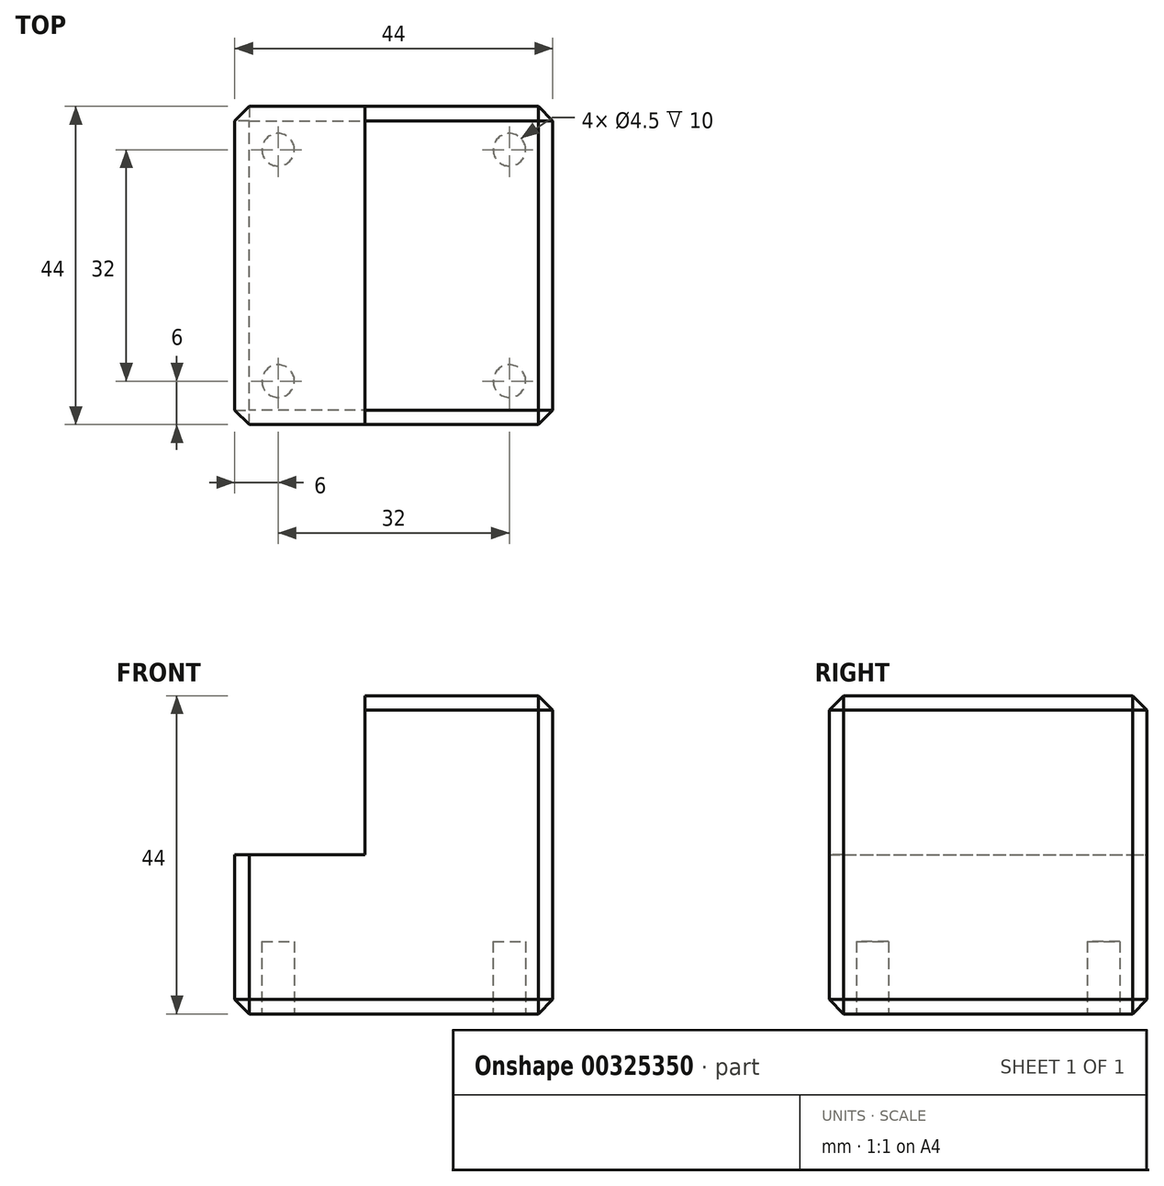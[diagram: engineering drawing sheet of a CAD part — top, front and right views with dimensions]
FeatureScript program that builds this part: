
annotation { "Feature Type Name" : "Feature", "Feature Type Description" : "" }
export const myFeature = defineFeature(function(context is Context, id is Id, definition is map)
    precondition{}
    {
        {
            var Q0;
            Q0=qCreatedBy(makeId("Front.planeOp"),FACE);
            var sketch = newSketch(context, id + "F0", { "sketchPlane" : qUnion([Q0])});
            skLineSegment(sketch, "E0.bottom", {"start": v(22, 22) * mm, "end": v(-4, 22) * mm});
            skLineSegment(sketch, "E0.top", {"start": v(22, -22) * mm, "end": v(-22, -22) * mm});
            skLineSegment(sketch, "E0.left", {"start": v(22, 22) * mm, "end": v(22, -22) * mm});
            skLineSegment(sketch, "E0.right", {"start": v(-22, 0) * mm, "end": v(-22, -22) * mm});
            skPoint(sketch, "E0.middle", {"position": v(0, 0) * mm});
            skLineSegment(sketch, "E1.top", {"start": v(-22, 0) * mm, "end": v(-4, 0) * mm});
            skLineSegment(sketch, "E1.right", {"start": v(-4, 22) * mm, "end": v(-4, 0) * mm});
            skPoint(sketch, "E2.orphan", {"position": v(-22, 22) * mm});
            skSolve(sketch);
        }
        {
            var Q0;
            Q0 = qSketchRegion(id + "F0", true);
            extrude(context, id + "F1", {"entities" : qUnion([Q0]), "depth" : 22 * mm, "hasSecondDirection" : true, "secondDirectionOppositeDirection" : true, "secondDirectionDepth" : 22 * mm});
        }
        {
            var Q0;
            Q0=makeQuery(id+"F1.opExtrude","SWEPT_EDGE",EDGE,{"disambiguationData":[OSD([sQuery(id+"F0.wireOp",EDGE,"E0.bottom"),sQuery(id+"F0.wireOp",EDGE,"E0.left")])]});
            var Q1;
            Q1=makeQuery(id+"F1.opExtrude","CAP_EDGE",EDGE,{"disambiguationData":[OSD([sQuery(id+"F0.wireOp",EDGE,"E0.bottom")])],"isStart":false});
            var Q2;
            Q2=makeQuery(id+"F1.opExtrude","CAP_EDGE",EDGE,{"disambiguationData":[OSD([sQuery(id+"F0.wireOp",EDGE,"E0.bottom")])],"isStart":true});
            var Q3;
            Q3=makeQuery(id+"F1.opExtrude","CAP_EDGE",EDGE,{"disambiguationData":[OSD([sQuery(id+"F0.wireOp",EDGE,"E0.left")])],"isStart":true});
            var Q4;
            Q4=makeQuery(id+"F1.opExtrude","CAP_EDGE",EDGE,{"disambiguationData":[OSD([sQuery(id+"F0.wireOp",EDGE,"E0.left")])],"isStart":false});
            var Q5;
            Q5=makeQuery(id+"F1.opExtrude","CAP_EDGE",EDGE,{"disambiguationData":[OSD([sQuery(id+"F0.wireOp",EDGE,"E0.right")])],"isStart":false});
            var Q6;
            Q6=makeQuery(id+"F1.opExtrude","CAP_EDGE",EDGE,{"disambiguationData":[OSD([sQuery(id+"F0.wireOp",EDGE,"E0.right")])],"isStart":true});
            var Q7;
            Q7=makeQuery(id+"F1.opExtrude","SWEPT_EDGE",EDGE,{"disambiguationData":[OSD([sQuery(id+"F0.wireOp",EDGE,"E0.top"),sQuery(id+"F0.wireOp",EDGE,"E0.left")])]});
            var Q8;
            Q8=makeQuery(id+"F1.opExtrude","CAP_EDGE",EDGE,{"disambiguationData":[OSD([sQuery(id+"F0.wireOp",EDGE,"E0.top")])],"isStart":true});
            var Q9;
            Q9=makeQuery(id+"F1.opExtrude","CAP_EDGE",EDGE,{"disambiguationData":[OSD([sQuery(id+"F0.wireOp",EDGE,"E0.top")])],"isStart":false});
            var Q10;
            Q10=makeQuery(id+"F1.opExtrude","SWEPT_EDGE",EDGE,{"disambiguationData":[OSD([sQuery(id+"F0.wireOp",EDGE,"E0.top"),sQuery(id+"F0.wireOp",EDGE,"E0.right")])]});
            chamfer(context, id + "F2", {"entities" : qUnion([Q0, Q1, Q2, Q3, Q4, Q5, Q6, Q7, Q8, Q9, Q10]), "width" : 2 * mm, "tangentPropagation" : true});
        }
        {
            var Q0;
            Q0=makeQuery(id+"F1.opExtrude","SWEPT_FACE",FACE,{"disambiguationData":[OSD([sQuery(id+"F0.wireOp",EDGE,"E0.top")])]});
            var sketch = newSketch(context, id + "F3", { "sketchPlane" : qUnion([Q0])});
            skCircle(sketch, "E3", {"center": v(-16, 16) * mm, "radius": 2.25 * mm});
            skCircle(sketch, "E4.MirrorC", {"center": v(16, 16) * mm, "radius": 2.25 * mm});
            skCircle(sketch, "E5.MirrorC", {"center": v(16, -16) * mm, "radius": 2.25 * mm});
            skCircle(sketch, "E6.MirrorC", {"center": v(-16, -16) * mm, "radius": 2.25 * mm});
            skSolve(sketch);
        }
        {
            var Q0;
            Q0 = qSketchRegion(id + "F3", true);
            extrude(context, id + "F4", {"entities" : qUnion([Q0]), "operationType" : NewBodyOperationType.REMOVE, "oppositeDirection" : true, "depth" : 10 * mm});
        }
    });
